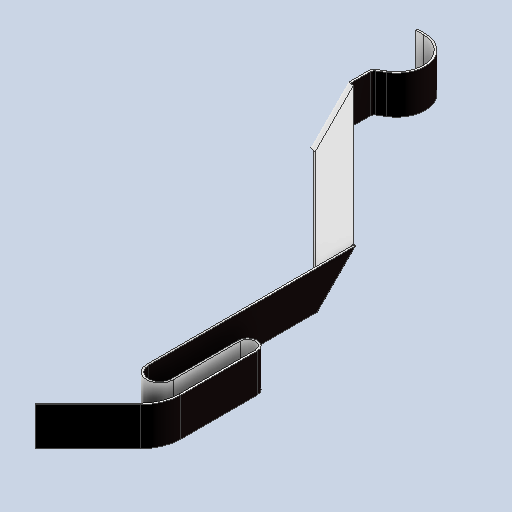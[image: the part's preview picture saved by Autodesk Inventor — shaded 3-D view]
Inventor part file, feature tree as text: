
AUTODESK INVENTOR PART (.ipt)
format: ipt  version: 2024.2 (Build 282272000, 272)  size: 226,816 bytes
history: native  units: mm
features: other x7, sketch x5, extrude x1
ambient origin geometry x8: Origin, YZ Plane, XZ Plane, XY Plane, X Axis, Y Axis, Z Axis, Center Point
bodies: Solid1 (feature_tree)
feature tree (13):
  extrude  "Extrusion1"  Depth=10.0mm
  other  "Bend Part1"
  other  "Bend Part19"
  other  "Bend Part20"
  other  "Bend Part21"
  other  "Bend Part22"
  other  "Bend Part23"
  other  "Bend Part24"
  sketch  "Sketch2"  dims[d0=200.0mm d1=10.0mm]
  sketch  "Sketch23"  dims[d2=0.5mm d3=0.0mm]
  sketch  "Sketch27"  dims[d4=2.0mm]
  sketch  "Sketch28"  dims[d5=7.0mm d6=150.0deg]
  sketch  "Sketch30"  dims[d69=1.0mm d70=60.0deg d71=2.0mm d72=45.0deg d73=5.0mm d74=0.1mm d75=180.0deg d76=45.0deg d77=26.0mm d78=0.1mm d79=180.0deg d80=3.0mm d81=180.0deg d82=2.0mm d83=180.0deg d84=10.0mm d85=45.0deg d86=20.0mm]
